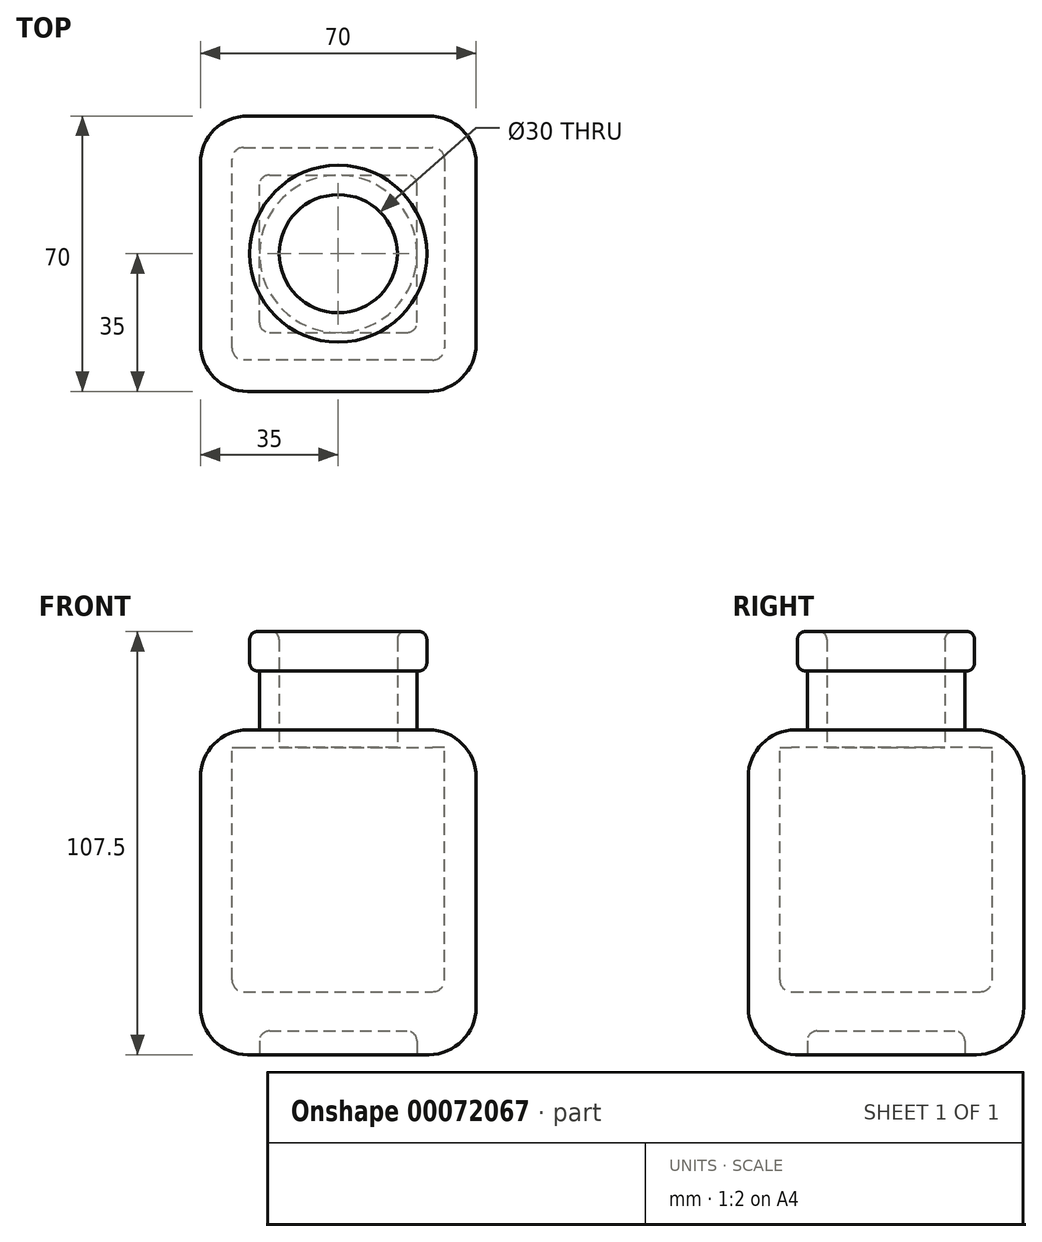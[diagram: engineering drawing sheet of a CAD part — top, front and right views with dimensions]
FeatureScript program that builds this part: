
annotation { "Feature Type Name" : "Feature", "Feature Type Description" : "" }
export const myFeature = defineFeature(function(context is Context, id is Id, definition is map)
    precondition{}
    {
        {
            var Q0;
            Q0=qCreatedBy(makeId("Top.planeOp"),FACE);
            var sketch = newSketch(context, id + "F0", { "sketchPlane" : qUnion([Q0])});
            skLineSegment(sketch, "E0.top", {"start": v(0, -35) * mm, "end": v(-35, -35) * mm});
            skLineSegment(sketch, "E0.right", {"start": v(-35, 0) * mm, "end": v(-35, -35) * mm});
            skLineSegment(sketch, "E1.MirrorCS", {"start": v(35, 0) * mm, "end": v(35, -35) * mm});
            skLineSegment(sketch, "E2.MirrorCS", {"start": v(0, -35) * mm, "end": v(35, -35) * mm});
            skLineSegment(sketch, "E3.MirrorCS", {"start": v(-35, 0) * mm, "end": v(-35, 35) * mm});
            skLineSegment(sketch, "E4.MirrorCS", {"start": v(35, 0) * mm, "end": v(35, 35) * mm});
            skLineSegment(sketch, "E5.MirrorCS", {"start": v(0, 35) * mm, "end": v(-35, 35) * mm});
            skLineSegment(sketch, "E6.MirrorCS", {"start": v(0, 35) * mm, "end": v(35, 35) * mm});
            skSolve(sketch);
        }
        {
            var Q0;
            Q0 = qSketchRegion(id + "F0", true);
            extrude(context, id + "F1", {"entities" : qUnion([Q0]), "oppositeDirection" : true, "depth" : 70 * mm});
        }
        {
            var Q0;
            Q0=makeQuery(id+"F1.opExtrude","CAP_FACE",FACE,{"disambiguationData":[OSD([sQuery(id+"F0.wireOp",EDGE,"E0.top"),sQuery(id+"F0.wireOp",EDGE,"E0.right"),sQuery(id+"F0.wireOp",EDGE,"E1.MirrorCS"),sQuery(id+"F0.wireOp",EDGE,"E2.MirrorCS"),sQuery(id+"F0.wireOp",EDGE,"E3.MirrorCS"),sQuery(id+"F0.wireOp",EDGE,"E4.MirrorCS"),sQuery(id+"F0.wireOp",EDGE,"E5.MirrorCS"),sQuery(id+"F0.wireOp",EDGE,"E6.MirrorCS")])],"isStart":true});
            shell(context, id + "F2", {"entities" : qUnion([Q0]), "thickness" : 8 * mm});
        }
        {
            var Q0;
            Q0=makeQuery(id+"F1.opExtrude","CAP_FACE",FACE,{"disambiguationData":[OSD([sQuery(id+"F0.wireOp",EDGE,"E0.top"),sQuery(id+"F0.wireOp",EDGE,"E0.right"),sQuery(id+"F0.wireOp",EDGE,"E1.MirrorCS"),sQuery(id+"F0.wireOp",EDGE,"E2.MirrorCS"),sQuery(id+"F0.wireOp",EDGE,"E3.MirrorCS"),sQuery(id+"F0.wireOp",EDGE,"E4.MirrorCS"),sQuery(id+"F0.wireOp",EDGE,"E5.MirrorCS"),sQuery(id+"F0.wireOp",EDGE,"E6.MirrorCS")])],"isStart":true});
            var sketch = newSketch(context, id + "F3", { "sketchPlane" : qUnion([Q0])});
            skLineSegment(sketch, "E7.bottom", {"start": v(-35, 35) * mm, "end": v(35, 35) * mm});
            skLineSegment(sketch, "E7.top", {"start": v(-35, -35) * mm, "end": v(35, -35) * mm});
            skLineSegment(sketch, "E7.left", {"start": v(-35, 35) * mm, "end": v(-35, -35) * mm});
            skLineSegment(sketch, "E7.right", {"start": v(35, 35) * mm, "end": v(35, -35) * mm});
            skCircle(sketch, "E8", {"center": v(0, 0) * mm, "radius": 15 * mm});
            skSolve(sketch);
        }
        {
            var Q0;
            Q0 = qSketchRegion(id + "F3", true);
            extrude(context, id + "F4", {"entities" : qUnion([Q0]), "operationType" : NewBodyOperationType.ADD, "depth" : 4.5 * mm});
        }
        {
            var Q0;
            Q0=makeQuery(id+"F4.opExtrude","CAP_FACE",FACE,{"disambiguationData":[OSD([sQuery(id+"F3.wireOp",EDGE,"E7.bottom"),sQuery(id+"F3.wireOp",EDGE,"E7.top"),sQuery(id+"F3.wireOp",EDGE,"E7.left"),sQuery(id+"F3.wireOp",EDGE,"E7.right"),sQuery(id+"F3.wireOp",EDGE,"E8")])],"isStart":false});
            var sketch = newSketch(context, id + "F5", { "sketchPlane" : qUnion([Q0])});
            skCircle(sketch, "E9", {"center": v(0, 0) * mm, "radius": 15 * mm});
            skCircle(sketch, "E10", {"center": v(0, 0) * mm, "radius": 20 * mm});
            skSolve(sketch);
        }
        {
            var Q0;
            Q0 = qSketchRegion(id + "F5", true);
            extrude(context, id + "F6", {"entities" : qUnion([Q0]), "operationType" : NewBodyOperationType.ADD, "depth" : 15 * mm});
        }
        {
            var Q0;
            Q0=makeQuery(id+"F6.opExtrude","CAP_FACE",FACE,{"disambiguationData":[OSD([sQuery(id+"F5.wireOp",EDGE,"E9"),sQuery(id+"F5.wireOp",EDGE,"E10")])],"isStart":false});
            var sketch = newSketch(context, id + "F7", { "sketchPlane" : qUnion([Q0])});
            skCircle(sketch, "E11", {"center": v(0, 0) * mm, "radius": 22.5 * mm});
            skCircle(sketch, "E12", {"center": v(0, 0) * mm, "radius": 15 * mm});
            skSolve(sketch);
        }
        {
            var Q0;
            Q0 = qSketchRegion(id + "F7", true);
            extrude(context, id + "F8", {"entities" : qUnion([Q0]), "operationType" : NewBodyOperationType.ADD, "depth" : 10 * mm});
        }
        {
            var Q0;
            Q0=makeQuery(id+"F1.opExtrude","CAP_FACE",FACE,{"disambiguationData":[OSD([sQuery(id+"F0.wireOp",EDGE,"E0.top"),sQuery(id+"F0.wireOp",EDGE,"E0.right"),sQuery(id+"F0.wireOp",EDGE,"E1.MirrorCS"),sQuery(id+"F0.wireOp",EDGE,"E2.MirrorCS"),sQuery(id+"F0.wireOp",EDGE,"E3.MirrorCS"),sQuery(id+"F0.wireOp",EDGE,"E4.MirrorCS"),sQuery(id+"F0.wireOp",EDGE,"E5.MirrorCS"),sQuery(id+"F0.wireOp",EDGE,"E6.MirrorCS")])],"isStart":false});
            var sketch = newSketch(context, id + "F9", { "sketchPlane" : qUnion([Q0])});
            skLineSegment(sketch, "E13.bottom", {"start": v(-35, 35) * mm, "end": v(35, 35) * mm});
            skLineSegment(sketch, "E13.top", {"start": v(-35, -35) * mm, "end": v(35, -35) * mm});
            skLineSegment(sketch, "E13.left", {"start": v(-35, 35) * mm, "end": v(-35, -35) * mm});
            skLineSegment(sketch, "E13.right", {"start": v(35, 35) * mm, "end": v(35, -35) * mm});
            skSolve(sketch);
        }
        {
            var Q0;
            Q0 = qSketchRegion(id + "F9", true);
            extrude(context, id + "F10", {"entities" : qUnion([Q0]), "operationType" : NewBodyOperationType.ADD, "depth" : 8 * mm});
        }
        {
            var Q0;
            Q0=makeQuery(id+"F10.opExtrude","CAP_FACE",FACE,{"disambiguationData":[OSD([sQuery(id+"F9.wireOp",EDGE,"E13.bottom"),sQuery(id+"F9.wireOp",EDGE,"E13.top"),sQuery(id+"F9.wireOp",EDGE,"E13.left"),sQuery(id+"F9.wireOp",EDGE,"E13.right")])],"isStart":false});
            var sketch = newSketch(context, id + "F11", { "sketchPlane" : qUnion([Q0])});
            skLineSegment(sketch, "E14", {"start": v(0, 56.68) * mm, "end": v(0, -55.93) * mm, "construction": true});
            skLineSegment(sketch, "E15", {"start": v(-45.64, 0) * mm, "end": v(51.91, 0) * mm, "construction": true});
            skLineSegment(sketch, "E16.bottom", {"start": v(-20, 20) * mm, "end": v(20, 20) * mm});
            skLineSegment(sketch, "E16.top", {"start": v(-20, -20) * mm, "end": v(20, -20) * mm});
            skLineSegment(sketch, "E16.left", {"start": v(-20, 20) * mm, "end": v(-20, -20) * mm});
            skLineSegment(sketch, "E16.right", {"start": v(20, 20) * mm, "end": v(20, -20) * mm});
            skSolve(sketch);
        }
        {
            var Q0;
            Q0 = qSketchRegion(id + "F11", true);
            extrude(context, id + "F12", {"entities" : qUnion([Q0]), "operationType" : NewBodyOperationType.REMOVE, "oppositeDirection" : true, "depth" : 6 * mm});
        }
        {
            var Q0;
            Q0=makeQuery(id+"F10.boolean.opBoolean","MERGE",EDGE,{"derivedFrom":[makeQuery(id+"F4.boolean.opBoolean","MERGE",EDGE,{"derivedFrom":[makeQuery(id+"F1.opExtrude","SWEPT_EDGE",EDGE,{"disambiguationData":[OSD([sQuery(id+"F0.wireOp",EDGE,"E1.MirrorCS"),sQuery(id+"F0.wireOp",EDGE,"E2.MirrorCS")])]}),makeQuery(id+"F4.opExtrude","SWEPT_EDGE",EDGE,{"disambiguationData":[OSD([sQuery(id+"F3.wireOp",EDGE,"E7.top"),sQuery(id+"F3.wireOp",EDGE,"E7.right")])]})]}),makeQuery(id+"F10.opExtrude","SWEPT_EDGE",EDGE,{"disambiguationData":[OSD([sQuery(id+"F9.wireOp",EDGE,"E13.bottom"),sQuery(id+"F9.wireOp",EDGE,"E13.right")])]})]});
            var Q1;
            Q1=makeQuery(id+"F10.opExtrude","CAP_EDGE",EDGE,{"disambiguationData":[OSD([sQuery(id+"F9.wireOp",EDGE,"E13.bottom")])],"isStart":false});
            var Q2;
            Q2=makeQuery(id+"F10.boolean.opBoolean","MERGE",EDGE,{"derivedFrom":[makeQuery(id+"F4.boolean.opBoolean","MERGE",EDGE,{"derivedFrom":[makeQuery(id+"F1.opExtrude","SWEPT_EDGE",EDGE,{"disambiguationData":[OSD([sQuery(id+"F0.wireOp",EDGE,"E0.top"),sQuery(id+"F0.wireOp",EDGE,"E0.right")])]}),makeQuery(id+"F4.opExtrude","SWEPT_EDGE",EDGE,{"disambiguationData":[OSD([sQuery(id+"F3.wireOp",EDGE,"E7.top"),sQuery(id+"F3.wireOp",EDGE,"E7.left")])]})]}),makeQuery(id+"F10.opExtrude","SWEPT_EDGE",EDGE,{"disambiguationData":[OSD([sQuery(id+"F9.wireOp",EDGE,"E13.bottom"),sQuery(id+"F9.wireOp",EDGE,"E13.left")])]})]});
            var Q3;
            Q3=makeQuery(id+"F10.opExtrude","CAP_EDGE",EDGE,{"disambiguationData":[OSD([sQuery(id+"F9.wireOp",EDGE,"E13.left")])],"isStart":false});
            var Q4;
            Q4=makeQuery(id+"F10.boolean.opBoolean","MERGE",EDGE,{"derivedFrom":[makeQuery(id+"F4.boolean.opBoolean","MERGE",EDGE,{"derivedFrom":[makeQuery(id+"F1.opExtrude","SWEPT_EDGE",EDGE,{"disambiguationData":[OSD([sQuery(id+"F0.wireOp",EDGE,"E3.MirrorCS"),sQuery(id+"F0.wireOp",EDGE,"E5.MirrorCS")])]}),makeQuery(id+"F4.opExtrude","SWEPT_EDGE",EDGE,{"disambiguationData":[OSD([sQuery(id+"F3.wireOp",EDGE,"E7.bottom"),sQuery(id+"F3.wireOp",EDGE,"E7.left")])]})]}),makeQuery(id+"F10.opExtrude","SWEPT_EDGE",EDGE,{"disambiguationData":[OSD([sQuery(id+"F9.wireOp",EDGE,"E13.top"),sQuery(id+"F9.wireOp",EDGE,"E13.left")])]})]});
            var Q5;
            Q5=makeQuery(id+"F10.opExtrude","CAP_EDGE",EDGE,{"disambiguationData":[OSD([sQuery(id+"F9.wireOp",EDGE,"E13.top")])],"isStart":false});
            var Q6;
            Q6=makeQuery(id+"F10.boolean.opBoolean","MERGE",EDGE,{"derivedFrom":[makeQuery(id+"F4.boolean.opBoolean","MERGE",EDGE,{"derivedFrom":[makeQuery(id+"F1.opExtrude","SWEPT_EDGE",EDGE,{"disambiguationData":[OSD([sQuery(id+"F0.wireOp",EDGE,"E4.MirrorCS"),sQuery(id+"F0.wireOp",EDGE,"E6.MirrorCS")])]}),makeQuery(id+"F4.opExtrude","SWEPT_EDGE",EDGE,{"disambiguationData":[OSD([sQuery(id+"F3.wireOp",EDGE,"E7.bottom"),sQuery(id+"F3.wireOp",EDGE,"E7.right")])]})]}),makeQuery(id+"F10.opExtrude","SWEPT_EDGE",EDGE,{"disambiguationData":[OSD([sQuery(id+"F9.wireOp",EDGE,"E13.top"),sQuery(id+"F9.wireOp",EDGE,"E13.right")])]})]});
            var Q7;
            Q7=makeQuery(id+"F10.opExtrude","CAP_EDGE",EDGE,{"disambiguationData":[OSD([sQuery(id+"F9.wireOp",EDGE,"E13.right")])],"isStart":false});
            var Q8;
            Q8=makeQuery(id+"F4.opExtrude","CAP_EDGE",EDGE,{"disambiguationData":[OSD([sQuery(id+"F3.wireOp",EDGE,"E7.right")])],"isStart":false});
            var Q9;
            Q9=makeQuery(id+"F4.opExtrude","CAP_EDGE",EDGE,{"disambiguationData":[OSD([sQuery(id+"F3.wireOp",EDGE,"E7.bottom")])],"isStart":false});
            var Q10;
            Q10=makeQuery(id+"F4.opExtrude","CAP_EDGE",EDGE,{"disambiguationData":[OSD([sQuery(id+"F3.wireOp",EDGE,"E7.left")])],"isStart":false});
            var Q11;
            Q11=makeQuery(id+"F4.opExtrude","CAP_EDGE",EDGE,{"disambiguationData":[OSD([sQuery(id+"F3.wireOp",EDGE,"E7.top")])],"isStart":false});
            fillet(context, id + "F13", {"entities" : qUnion([Q0, Q1, Q2, Q3, Q4, Q5, Q6, Q7, Q8, Q9, Q10, Q11]), "radius" : 12 * mm, "tangentPropagation" : true, "allowEdgeOverflow" : false});
        }
        {
            var Q0;
            Q0=makeQuery(id+"F8.opExtrude","CAP_EDGE",EDGE,{"disambiguationData":[OSD([sQuery(id+"F7.wireOp",EDGE,"E11")])],"isStart":false});
            var Q1;
            Q1=makeQuery(id+"F8.opExtrude","CAP_EDGE",EDGE,{"disambiguationData":[OSD([sQuery(id+"F7.wireOp",EDGE,"E11")])],"isStart":true});
            var Q2;
            Q2=makeQuery(id+"F8.opExtrude","CAP_EDGE",EDGE,{"disambiguationData":[OSD([sQuery(id+"F7.wireOp",EDGE,"E12")])],"isStart":false});
            fillet(context, id + "F14", {"entities" : qUnion([Q0, Q1, Q2]), "radius" : 2 * mm, "tangentPropagation" : true, "allowEdgeOverflow" : false});
        }
        {
            var Q0;
            Q0=makeQuery(id+"F12.boolean.opBoolean","COPY",EDGE,{"derivedFrom":makeQuery(id+"F12.opExtrude","CAP_EDGE",EDGE,{"disambiguationData":[OSD([sQuery(id+"F11.wireOp",EDGE,"E16.top")])],"isStart":true})});
            var Q1;
            Q1=makeQuery(id+"F12.boolean.opBoolean","COPY",EDGE,{"derivedFrom":makeQuery(id+"F12.opExtrude","CAP_EDGE",EDGE,{"disambiguationData":[OSD([sQuery(id+"F11.wireOp",EDGE,"E16.left")])],"isStart":true})});
            var Q2;
            Q2=makeQuery(id+"F12.boolean.opBoolean","COPY",EDGE,{"derivedFrom":makeQuery(id+"F12.opExtrude","CAP_EDGE",EDGE,{"disambiguationData":[OSD([sQuery(id+"F11.wireOp",EDGE,"E16.bottom")])],"isStart":true})});
            var Q3;
            Q3=makeQuery(id+"F12.boolean.opBoolean","COPY",EDGE,{"derivedFrom":makeQuery(id+"F12.opExtrude","CAP_EDGE",EDGE,{"disambiguationData":[OSD([sQuery(id+"F11.wireOp",EDGE,"E16.right")])],"isStart":true})});
            var Q4;
            Q4=makeQuery(id+"F12.boolean.opBoolean","COPY",EDGE,{"derivedFrom":makeQuery(id+"F12.opExtrude","CAP_EDGE",EDGE,{"disambiguationData":[OSD([sQuery(id+"F11.wireOp",EDGE,"E16.top")])],"isStart":false})});
            var Q5;
            Q5=makeQuery(id+"F12.boolean.opBoolean","COPY",EDGE,{"derivedFrom":makeQuery(id+"F12.opExtrude","CAP_EDGE",EDGE,{"disambiguationData":[OSD([sQuery(id+"F11.wireOp",EDGE,"E16.left")])],"isStart":false})});
            var Q6;
            Q6=makeQuery(id+"F12.boolean.opBoolean","COPY",EDGE,{"derivedFrom":makeQuery(id+"F12.opExtrude","CAP_EDGE",EDGE,{"disambiguationData":[OSD([sQuery(id+"F11.wireOp",EDGE,"E16.bottom")])],"isStart":false})});
            var Q7;
            Q7=makeQuery(id+"F12.boolean.opBoolean","COPY",EDGE,{"derivedFrom":makeQuery(id+"F12.opExtrude","CAP_EDGE",EDGE,{"disambiguationData":[OSD([sQuery(id+"F11.wireOp",EDGE,"E16.right")])],"isStart":false})});
            var Q8;
            Q8=makeQuery(id+"F12.boolean.opBoolean","COPY",EDGE,{"derivedFrom":makeQuery(id+"F12.opExtrude","SWEPT_EDGE",EDGE,{"disambiguationData":[OSD([sQuery(id+"F11.wireOp",EDGE,"E16.top"),sQuery(id+"F11.wireOp",EDGE,"E16.left")])]})});
            var Q9;
            Q9=makeQuery(id+"F12.boolean.opBoolean","COPY",EDGE,{"derivedFrom":makeQuery(id+"F12.opExtrude","SWEPT_EDGE",EDGE,{"disambiguationData":[OSD([sQuery(id+"F11.wireOp",EDGE,"E16.bottom"),sQuery(id+"F11.wireOp",EDGE,"E16.left")])]})});
            var Q10;
            Q10=makeQuery(id+"F12.boolean.opBoolean","COPY",EDGE,{"derivedFrom":makeQuery(id+"F12.opExtrude","SWEPT_EDGE",EDGE,{"disambiguationData":[OSD([sQuery(id+"F11.wireOp",EDGE,"E16.top"),sQuery(id+"F11.wireOp",EDGE,"E16.right")])]})});
            var Q11;
            Q11=makeQuery(id+"F12.boolean.opBoolean","COPY",EDGE,{"derivedFrom":makeQuery(id+"F12.opExtrude","SWEPT_EDGE",EDGE,{"disambiguationData":[OSD([sQuery(id+"F11.wireOp",EDGE,"E16.bottom"),sQuery(id+"F11.wireOp",EDGE,"E16.right")])]})});
            fillet(context, id + "F15", {"entities" : qUnion([Q0, Q1, Q2, Q3, Q4, Q5, Q6, Q7, Q8, Q9, Q10, Q11]), "radius" : 2.5 * mm, "tangentPropagation" : true, "allowEdgeOverflow" : false});
        }
        {
            var Q0;
            {var subQ0=sQuery(id+"F0.wireOp",EDGE,"E4.MirrorCS");var subQ1=sQuery(id+"F0.wireOp",EDGE,"E1.MirrorCS");Q0=makeQuery(id+"F2.opShell","OFFSET_EDGE",EDGE,{"disambiguationData":[OSD([subQ1,subQ0]),TDD([makeQuery(id+"F1.opExtrude","CAP_EDGE",EDGE,{"disambiguationData":[OSD([subQ1,subQ0])],"isStart":false})])]});}
            var Q1;
            Q1=makeQuery(id+"F2.opShell","OFFSET_EDGE",EDGE,{"disambiguationData":[OSD([sQuery(id+"F0.wireOp",EDGE,"E1.MirrorCS"),sQuery(id+"F0.wireOp",EDGE,"E2.MirrorCS")])]});
            var Q2;
            {var subQ0=sQuery(id+"F0.wireOp",EDGE,"E2.MirrorCS");var subQ1=sQuery(id+"F0.wireOp",EDGE,"E0.top");Q2=makeQuery(id+"F2.opShell","OFFSET_EDGE",EDGE,{"disambiguationData":[OSD([subQ1,subQ0]),TDD([makeQuery(id+"F1.opExtrude","CAP_EDGE",EDGE,{"disambiguationData":[OSD([subQ1,subQ0])],"isStart":true})])]});}
            var Q3;
            Q3=makeQuery(id+"F2.opShell","OFFSET_EDGE",EDGE,{"disambiguationData":[OSD([sQuery(id+"F0.wireOp",EDGE,"E0.top"),sQuery(id+"F0.wireOp",EDGE,"E0.right")])]});
            var Q4;
            {var subQ0=sQuery(id+"F0.wireOp",EDGE,"E3.MirrorCS");var subQ1=sQuery(id+"F0.wireOp",EDGE,"E0.right");Q4=makeQuery(id+"F2.opShell","OFFSET_EDGE",EDGE,{"disambiguationData":[OSD([subQ1,subQ0]),TDD([makeQuery(id+"F1.opExtrude","CAP_EDGE",EDGE,{"disambiguationData":[OSD([subQ1,subQ0])],"isStart":false})])]});}
            var Q5;
            {var subQ0=sQuery(id+"F0.wireOp",EDGE,"E3.MirrorCS");var subQ1=sQuery(id+"F0.wireOp",EDGE,"E0.right");Q5=makeQuery(id+"F2.opShell","OFFSET_EDGE",EDGE,{"disambiguationData":[OSD([subQ1,subQ0]),TDD([makeQuery(id+"F1.opExtrude","CAP_EDGE",EDGE,{"disambiguationData":[OSD([subQ1,subQ0])],"isStart":true})])]});}
            var Q6;
            Q6=makeQuery(id+"F2.opShell","OFFSET_EDGE",EDGE,{"disambiguationData":[OSD([sQuery(id+"F0.wireOp",EDGE,"E3.MirrorCS"),sQuery(id+"F0.wireOp",EDGE,"E5.MirrorCS")])]});
            var Q7;
            {var subQ0=sQuery(id+"F0.wireOp",EDGE,"E6.MirrorCS");var subQ1=sQuery(id+"F0.wireOp",EDGE,"E5.MirrorCS");Q7=makeQuery(id+"F2.opShell","OFFSET_EDGE",EDGE,{"disambiguationData":[OSD([subQ1,subQ0]),TDD([makeQuery(id+"F1.opExtrude","CAP_EDGE",EDGE,{"disambiguationData":[OSD([subQ1,subQ0])],"isStart":true})])]});}
            var Q8;
            {var subQ0=sQuery(id+"F0.wireOp",EDGE,"E6.MirrorCS");var subQ1=sQuery(id+"F0.wireOp",EDGE,"E5.MirrorCS");Q8=makeQuery(id+"F2.opShell","OFFSET_EDGE",EDGE,{"disambiguationData":[OSD([subQ1,subQ0]),TDD([makeQuery(id+"F1.opExtrude","CAP_EDGE",EDGE,{"disambiguationData":[OSD([subQ1,subQ0])],"isStart":false})])]});}
            var Q9;
            {var subQ0=sQuery(id+"F0.wireOp",EDGE,"E2.MirrorCS");var subQ1=sQuery(id+"F0.wireOp",EDGE,"E0.top");Q9=makeQuery(id+"F2.opShell","OFFSET_EDGE",EDGE,{"disambiguationData":[OSD([subQ1,subQ0]),TDD([makeQuery(id+"F1.opExtrude","CAP_EDGE",EDGE,{"disambiguationData":[OSD([subQ1,subQ0])],"isStart":false})])]});}
            var Q10;
            Q10=makeQuery(id+"F2.opShell","OFFSET_EDGE",EDGE,{"disambiguationData":[OSD([sQuery(id+"F0.wireOp",EDGE,"E4.MirrorCS"),sQuery(id+"F0.wireOp",EDGE,"E6.MirrorCS")])]});
            var Q11;
            {var subQ0=sQuery(id+"F0.wireOp",EDGE,"E4.MirrorCS");var subQ1=sQuery(id+"F0.wireOp",EDGE,"E1.MirrorCS");Q11=makeQuery(id+"F2.opShell","OFFSET_EDGE",EDGE,{"disambiguationData":[OSD([subQ1,subQ0]),TDD([makeQuery(id+"F1.opExtrude","CAP_EDGE",EDGE,{"disambiguationData":[OSD([subQ1,subQ0])],"isStart":true})])]});}
            fillet(context, id + "F16", {"entities" : qUnion([Q0, Q1, Q2, Q3, Q4, Q5, Q6, Q7, Q8, Q9, Q10, Q11]), "radius" : 3 * mm, "tangentPropagation" : true, "allowEdgeOverflow" : false});
        }
    });
